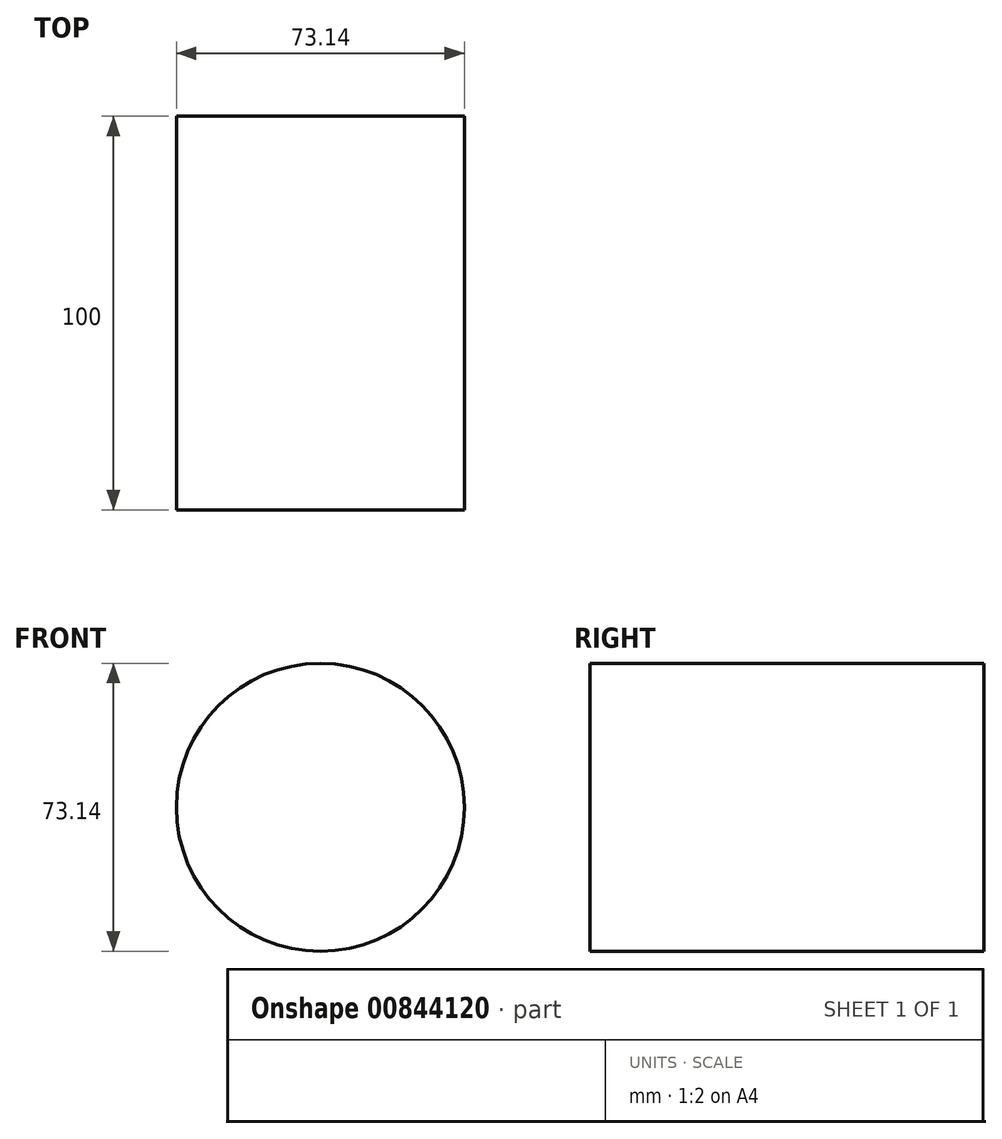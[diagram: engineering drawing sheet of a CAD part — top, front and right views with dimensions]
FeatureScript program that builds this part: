
annotation { "Feature Type Name" : "Feature", "Feature Type Description" : "" }
export const myFeature = defineFeature(function(context is Context, id is Id, definition is map)
    precondition{}
    {
        {
            var Q0;
            Q0=qCreatedBy(makeId("Front.planeOp"),FACE);
            var sketch = newSketch(context, id + "F0", { "sketchPlane" : qUnion([Q0])});
            skCircle(sketch, "E0", {"center": v(16.53, 0) * mm, "radius": 38.4 * mm});
            skCircle(sketch, "E1", {"center": v(36.65, 0) * mm, "radius": 22.73 * mm});
            skCircle(sketch, "E2", {"center": v(-68.75, -33.26) * mm, "radius": 36.57 * mm});
            skSolve(sketch);
        }
        {
            var Q0;
            Q0=makeQuery(id+"F0.imprint","IMPRINT",FACE,{"disambiguationData":[TD([[makeQuery(id+"F0.imprint","IMPRINT",EDGE,{"derivedFrom":sQuery(id+"F0.wireOp",EDGE,"E2")}),1.0]])]});
            extrude(context, id + "F1", {"entities" : qUnion([Q0]), "depth" : 100 * mm, "offsetDistance" : 25.4 * mm});
        }
        {
            var Q0;
            Q0=makeQuery(id+"F1.opExtrude","CAP_FACE",FACE,{"disambiguationData":[OSD([sQuery(id+"F0.wireOp",EDGE,"E2")])],"isStart":false});
            var sketch = newSketch(context, id + "F2", { "sketchPlane" : qUnion([Q0])});
            skLineSegment(sketch, "E3.bottom", {"start": v(-50.39, -15.95) * mm, "end": v(-87.12, -15.95) * mm});
            skLineSegment(sketch, "E3.top", {"start": v(-50.39, -50.57) * mm, "end": v(-87.12, -50.57) * mm});
            skLineSegment(sketch, "E3.left", {"start": v(-50.39, -15.95) * mm, "end": v(-50.39, -50.57) * mm});
            skLineSegment(sketch, "E3.right", {"start": v(-87.12, -15.95) * mm, "end": v(-87.12, -50.57) * mm});
            skPoint(sketch, "E3.middle", {"position": v(-68.75, -33.26) * mm});
            skSolve(sketch);
        }
        {
            var Q0;
            Q0=makeQuery(id+"F2.imprint","IMPRINT",FACE,{"disambiguationData":[TD([[makeQuery(id+"F2.imprint","IMPRINT",EDGE,{"derivedFrom":sQuery(id+"F2.wireOp",EDGE,"E3.bottom")}),1.0]])]});
            extrude(context, id + "F3", {"entities" : qUnion([Q0]), "operationType" : NewBodyOperationType.ADD, "oppositeDirection" : true, "depth" : 100 * mm, "offsetDistance" : 25.4 * mm});
        }
    });
